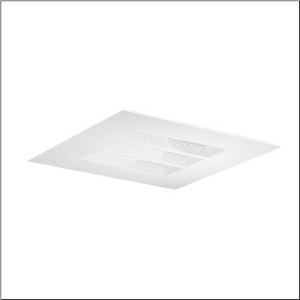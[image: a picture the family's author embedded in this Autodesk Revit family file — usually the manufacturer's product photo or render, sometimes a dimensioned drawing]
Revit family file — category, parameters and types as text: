
# Revit family: taris_r__21_51mt1lv0jhgddb02_0026
name_source: partatom
category: Lighting Fixtures
units: mm (PartAtom-declared; Revit-internal decimal feet)

## family parameters
Cut with Voids When Loaded = No
Host = Face
Light Source = No
Part Type = Normal
Room Calculation Point = No
Round Connector Dimension = Use Diameter
Shared = No

## types (1)
- Taris® 21 (1 x LED, 4620 lm, 31.1 W, 4000K)
    Apparent Load = 31 VA
    CIE Flux Codes = 79 97 100 100 100
    Color Rendering = 80
    Color Temperature = 4000K
    Default Elevation = 1800 mm
    Description = Taris® 21, office luminaire, primary anti-glare with micro louvre, primary optical cover: axial lens, of PMMA, structured, CAT 2 (L<= 1500cd/m²), light emission: direct distribution, primary light characteristic: symmetric, installation type: lay-in mounting, LED rated luminous flux: 4.620 lm, light colour: 840, colour temperature: 4000K, control gear: ECG, with terminal, 3-pole, mains connection: 230V, AC, 50Hz, rated input power: 31W, housing, luminaire housing, of plastic, traffic white (RAL 9016), module: M625, length: 622 mm, width: 622 mm, height: 42mm, protection rating (complete): IP20, insulation class (complete): insulation class I (protective earthing), certification: CE, ENEC, VDE, protection symbol: F, impact resistance: IK02, permissible ambient temperature for indoor applications: 0..+35°C, standard: EN 50419, packaging unit: 1 piece
    Height = 0 mm  [stored 0 ft]
    Lamp = 1 x LED
    Lamp Light Flux = 4620 lm
    Lamp Power = 31.1 W
    Lamp count = 1
    Length = 622 mm
    Luminous efficacy = 149 lm/W
    Manufacturer = Siteco
    ModVariant = No
    Model = 51MT1LV0JHGDDB02
    Mounting Place = Ceiling
    Mounting Type = Recessed
    Number of Poles = 1
    OnlyDefault = Yes
    Power Factor = 1
    Product Name = Taris® 21
    Product group = office luminaire | ceiling recessed
    ProductGroupID = 400
    Protection Class = Protection class I
    Protection Degree = IP 20
    RLX_Detail_Level = 1
    RlxData = <blob elided: 19573 chars, md5=811ed02f>
    Socket = socket
    Standby Power = 0 W
    System Light Flux = 4620 lm
    System Power = 31 W
    Type Comments = Product without accessories
    Type Image = l_1004820.jpg
    URL = http://relux.com
    VarID = ---
    Voltage = 0 V
    Weight = 0.00 kg
    Width = 622 mm

note: [stored X ft] marks values corroborated as IEEE doubles in the binary element streams (Revit-internal decimal feet)

## geometry (parser evidence)
native form markers: Blend x4, Sweep x12
no freeform markers — native parametric forms only
